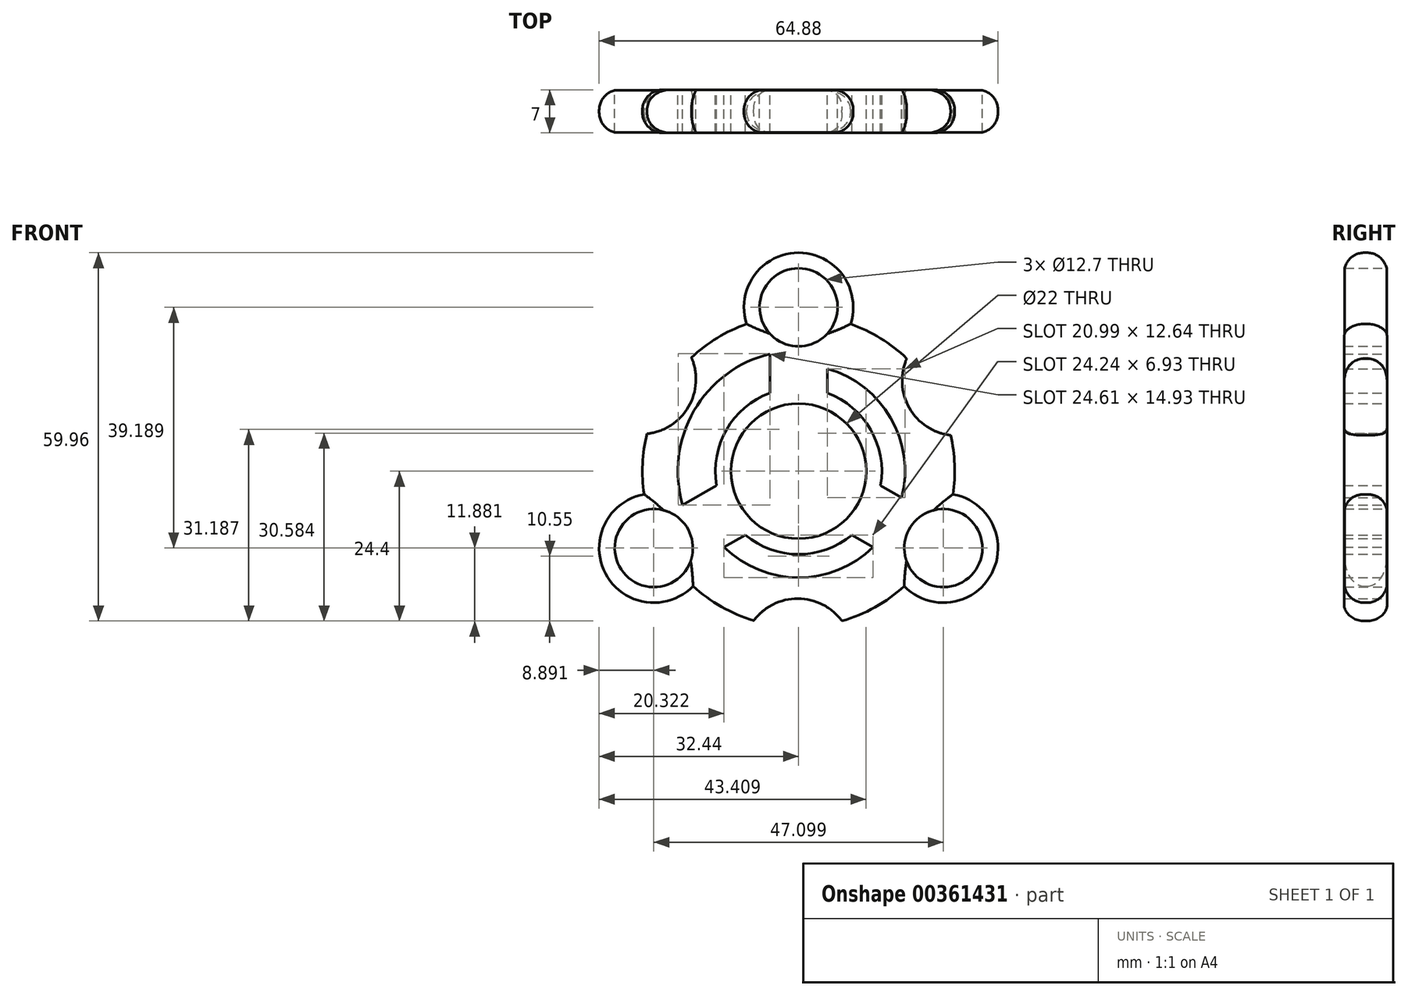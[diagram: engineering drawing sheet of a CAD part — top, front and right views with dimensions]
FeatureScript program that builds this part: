
annotation { "Feature Type Name" : "Feature", "Feature Type Description" : "" }
export const myFeature = defineFeature(function(context is Context, id is Id, definition is map)
    precondition{}
    {
        {
            var Q0;
            Q0=qCreatedBy(makeId("Front.planeOp"),FACE);
            var sketch = newSketch(context, id + "F0", { "sketchPlane" : qUnion([Q0])});
            skCircle(sketch, "E0", {"center": v(0, 0) * mm, "radius": 11 * mm});
            skCircle(sketch, "E1", {"center": v(0, 0) * mm, "radius": 25.4 * mm});
            skCircle(sketch, "E2", {"center": v(-23.55, -12.52) * mm, "radius": 6.35 * mm});
            skCircle(sketch, "E3", {"center": v(-23.55, -12.52) * mm, "radius": 8.9 * mm});
            skCircle(sketch, "E4", {"center": v(23.55, -12.52) * mm, "radius": 6.35 * mm});
            skCircle(sketch, "E5", {"center": v(23.55, -12.52) * mm, "radius": 8.9 * mm});
            skCircle(sketch, "E6", {"center": v(0, 26.67) * mm, "radius": 6.35 * mm});
            skCircle(sketch, "E7", {"center": v(0, 26.67) * mm, "radius": 8.9 * mm});
            skCircle(sketch, "E8", {"center": v(0, 0) * mm, "radius": 52.92 * mm});
            skCircle(sketch, "E9", {"center": v(0, 0) * mm, "radius": 35.56 * mm});
            skCircle(sketch, "E10", {"center": v(0, 0) * mm, "radius": 19.65 * mm});
            skCircle(sketch, "E11", {"center": v(0, 0) * mm, "radius": 17.32 * mm});
            skLineSegment(sketch, "E12", {"start": v(-4.65, 19.1) * mm, "end": v(-4.65, 9.97) * mm});
            skLineSegment(sketch, "E13", {"start": v(0, 0) * mm, "end": v(0, 14.53) * mm});
            skLineSegment(sketch, "E14.MirrorCS", {"start": v(4.65, 19.1) * mm, "end": v(4.65, 9.97) * mm});
            skLineSegment(sketch, "E15.1.0", {"start": v(-14.21, -13.57) * mm, "end": v(-6.3, -9.01) * mm});
            skLineSegment(sketch, "E15.1.1", {"start": v(-18.86, -5.52) * mm, "end": v(-10.96, -0.96) * mm});
            skLineSegment(sketch, "E15.2.0", {"start": v(18.86, -5.52) * mm, "end": v(10.96, -0.96) * mm});
            skLineSegment(sketch, "E15.2.1", {"start": v(14.21, -13.57) * mm, "end": v(6.3, -9.01) * mm});
            skCircle(sketch, "E16.0", {"center": v(0, 0) * mm, "radius": 13.54 * mm});
            skCircle(sketch, "E17", {"center": v(25.75, 14.7) * mm, "radius": 8.92 * mm});
            skCircle(sketch, "E18.1.0", {"center": v(-25.61, 14.95) * mm, "radius": 8.92 * mm});
            skCircle(sketch, "E18.2.0", {"center": v(-0.14, -29.66) * mm, "radius": 8.92 * mm});
            skSolve(sketch);
        }
        {
            var Q0;
            Q0=makeQuery(id+"F0.imprint","IMPRINT",FACE,{"disambiguationData":[TD([[makeQuery(id+"F0.imprint","IMPRINT",EDGE,{"derivedFrom":sQuery(id+"F0.wireOp",EDGE,"mSKZXrSF-bokL-tN16-Lumc-55fyRWtqHddJ")}),-1.0]])]});
            var Q1;
            {var subQ8=sQuery(id+"F0.wireOp",EDGE,"fPu7WKpn-9iuT-SH4j-aVLn-gu6anXdCReWU");Q1=makeQuery(id+"F0.imprint","IMPRINT",FACE,{"disambiguationData":[TD([[makeQuery(id+"F0.imprint","IMPRINT",EDGE,{"derivedFrom":subQ8}),1.0]])]});}
            var Q2;
            {var subQ3=sQuery(id+"F0.wireOp",EDGE,"4ilAvNyg-G02q-2Sgi-f1XK-hpsLkyDSZg0P");Q2=makeQuery(id+"F0.imprint","IMPRINT",FACE,{"disambiguationData":[TD([[makeQuery(id+"F0.imprint","IMPRINT",EDGE,{"derivedFrom":subQ3}),-1.0]])]});}
            var Q3;
            {var subQ0=sQuery(id+"F0.wireOp",EDGE,"f3iT29FV-d3kl-SGgA-KpPZ-BqzFadvLnQMr");var subQ1=sQuery(id+"F0.wireOp",EDGE,"k1AMuMOI-9OIa-mogb-beaB-4OQdduFXYsJP");var subQ2=makeQuery(id+"F0.imprint","INTERSECT",VERTEX,{"derivedFrom":[subQ1,subQ0]});Q3=makeQuery(id+"F0.imprint","IMPRINT",FACE,{"disambiguationData":[TD([[makeQuery(id+"F0.imprint","IMPRINT",EDGE,{"disambiguationData":[TD([[subQ2,-1.0]])],"derivedFrom":subQ1}),1.0]])]});}
            var Q4;
            {var subQ0=sQuery(id+"F0.wireOp",EDGE,"k1AMuMOI-9OIa-mogb-beaB-4OQdduFXYsJP");var subQ1=sQuery(id+"F0.wireOp",EDGE,"iGLwzaDJ-7IT3-vr1I-QoHF-4tAO6eRJBZaL");var subQ2=makeQuery(id+"F0.imprint","INTERSECT",VERTEX,{"disambiguationData":[OD(0.0)],"derivedFrom":[subQ1,subQ0]});Q4=makeQuery(id+"F0.imprint","IMPRINT",FACE,{"disambiguationData":[TD([[makeQuery(id+"F0.imprint","IMPRINT",EDGE,{"disambiguationData":[TD([[subQ2,-1.0]])],"derivedFrom":subQ1}),1.0]])]});}
            var Q5;
            {var subQ0=sQuery(id+"F0.wireOp",EDGE,"F0ToaT1C-rCX3-ocJg-bCzJ-bWa1iAX8OkwY");var subQ1=sQuery(id+"F0.wireOp",EDGE,"iGLwzaDJ-7IT3-vr1I-QoHF-4tAO6eRJBZaL");var subQ2=makeQuery(id+"F0.imprint","INTERSECT",VERTEX,{"disambiguationData":[OD(1.0)],"derivedFrom":[subQ1,subQ0]});Q5=makeQuery(id+"F0.imprint","IMPRINT",FACE,{"disambiguationData":[TD([[makeQuery(id+"F0.imprint","IMPRINT",EDGE,{"disambiguationData":[TD([[subQ2,-1.0]])],"derivedFrom":subQ1}),1.0]])]});}
            var Q6;
            {var subQ0=sQuery(id+"F0.wireOp",EDGE,"k1AMuMOI-9OIa-mogb-beaB-4OQdduFXYsJP");var subQ2=sQuery(id+"F0.wireOp",EDGE,"iGLwzaDJ-7IT3-vr1I-QoHF-4tAO6eRJBZaL");var subQ3=makeQuery(id+"F0.imprint","INTERSECT",VERTEX,{"disambiguationData":[OD(0.0)],"derivedFrom":[subQ2,subQ0]});Q6=makeQuery(id+"F0.imprint","IMPRINT",FACE,{"disambiguationData":[TD([[makeQuery(id+"F0.imprint","IMPRINT",EDGE,{"disambiguationData":[TD([[subQ3,-1.0]])],"derivedFrom":subQ2}),-1.0]])]});}
            var Q7;
            {var subQ0=sQuery(id+"F0.wireOp",EDGE,"Pe8qA6hG-RcvW-RrlY-0SVl-eZSLoO9VlF4p");Q7=makeQuery(id+"F0.imprint","IMPRINT",FACE,{"disambiguationData":[TD([[makeQuery(id+"F0.imprint","IMPRINT",EDGE,{"derivedFrom":subQ0}),1.0]])]});}
            var Q8;
            {var subQ3=sQuery(id+"F0.wireOp",EDGE,"SQ3UOjtt-CO0L-W6pf-Tdd5-0RniTD11PeOA");Q8=makeQuery(id+"F0.imprint","IMPRINT",FACE,{"disambiguationData":[TD([[makeQuery(id+"F0.imprint","IMPRINT",EDGE,{"derivedFrom":subQ3}),-1.0]])]});}
            var Q9;
            {var subQ0=sQuery(id+"F0.wireOp",EDGE,"4dQ9Bq4I-DzAn-Wkjs-vgun-b56G0d8Tkzou");Q9=makeQuery(id+"F0.imprint","IMPRINT",FACE,{"disambiguationData":[TD([[makeQuery(id+"F0.imprint","IMPRINT",EDGE,{"derivedFrom":subQ0}),1.0]])]});}
            var Q10;
            {var subQ3=sQuery(id+"F0.wireOp",EDGE,"QSqqfJXS-DOuh-B992-D5fL-yo85PLpnEcZw");Q10=makeQuery(id+"F0.imprint","IMPRINT",FACE,{"disambiguationData":[TD([[makeQuery(id+"F0.imprint","IMPRINT",EDGE,{"derivedFrom":subQ3}),-1.0]])]});}
            var Q11;
            {var subQ0=sQuery(id+"F0.wireOp",EDGE,"SBCOgly3-Q38N-qhpe-h8m8-IKpbl3d7nyb5");var subQ1=sQuery(id+"F0.wireOp",EDGE,"XELYKncj-OPtR-12Rn-Jsxf-ExqIg9yh0c7n");var subQ2=makeQuery(id+"F0.imprint","INTERSECT",VERTEX,{"derivedFrom":[subQ1,subQ0]});Q11=makeQuery(id+"F0.imprint","IMPRINT",FACE,{"disambiguationData":[TD([[makeQuery(id+"F0.imprint","IMPRINT",EDGE,{"disambiguationData":[TD([[subQ2,-1.0]])],"derivedFrom":subQ1}),1.0]])]});}
            var Q12;
            {var subQ0=sQuery(id+"F0.wireOp",EDGE,"f3iT29FV-d3kl-SGgA-KpPZ-BqzFadvLnQMr");var subQ1=sQuery(id+"F0.wireOp",EDGE,"8PpJuGD2-E3kl-GQEw-ypm4-Vkr7KxbCOpBG");var subQ2=makeQuery(id+"F0.imprint","INTERSECT",VERTEX,{"derivedFrom":[subQ1,subQ0]});Q12=makeQuery(id+"F0.imprint","IMPRINT",FACE,{"disambiguationData":[TD([[makeQuery(id+"F0.imprint","IMPRINT",EDGE,{"disambiguationData":[TD([[subQ2,1.0]])],"derivedFrom":subQ1}),1.0]])]});}
            var Q13;
            {var subQ0=sQuery(id+"F0.wireOp",EDGE,"FViSIV4C-5KW0-IByP-Mo0J-ua9ajbXaziPq");var subQ1=sQuery(id+"F0.wireOp",EDGE,"iGLwzaDJ-7IT3-vr1I-QoHF-4tAO6eRJBZaL");var subQ2=makeQuery(id+"F0.imprint","INTERSECT",VERTEX,{"disambiguationData":[OD(1.0)],"derivedFrom":[subQ1,subQ0]});Q13=makeQuery(id+"F0.imprint","IMPRINT",FACE,{"disambiguationData":[TD([[makeQuery(id+"F0.imprint","IMPRINT",EDGE,{"disambiguationData":[TD([[subQ2,-1.0]])],"derivedFrom":subQ1}),1.0]])]});}
            var Q14;
            {var subQ0=sQuery(id+"F0.wireOp",EDGE,"XELYKncj-OPtR-12Rn-Jsxf-ExqIg9yh0c7n");var subQ1=sQuery(id+"F0.wireOp",EDGE,"iGLwzaDJ-7IT3-vr1I-QoHF-4tAO6eRJBZaL");var subQ2=makeQuery(id+"F0.imprint","INTERSECT",VERTEX,{"disambiguationData":[OD(0.0)],"derivedFrom":[subQ1,subQ0]});Q14=makeQuery(id+"F0.imprint","IMPRINT",FACE,{"disambiguationData":[TD([[makeQuery(id+"F0.imprint","IMPRINT",EDGE,{"disambiguationData":[TD([[subQ2,-1.0]])],"derivedFrom":subQ1}),1.0]])]});}
            var Q15;
            Q15=makeQuery(id+"F0.imprint","IMPRINT",FACE,{"disambiguationData":[TD([[makeQuery(id+"F0.imprint","IMPRINT",EDGE,{"derivedFrom":sQuery(id+"F0.wireOp",EDGE,"1c7fcd95-4264-435f-8558-640e4e192e05.1.0")}),-1.0]])]});
            var Q16;
            Q16=makeQuery(id+"F0.imprint","IMPRINT",FACE,{"disambiguationData":[TD([[makeQuery(id+"F0.imprint","IMPRINT",EDGE,{"derivedFrom":sQuery(id+"F0.wireOp",EDGE,"30GUSKW5-8Tkx-gIO0-MBQh-iSdmt1q3Aj4F")}),-1.0]])]});
            var Q17;
            {var subQ0=sQuery(id+"F0.wireOp",EDGE,"8PpJuGD2-E3kl-GQEw-ypm4-Vkr7KxbCOpBG");var subQ1=sQuery(id+"F0.wireOp",EDGE,"iGLwzaDJ-7IT3-vr1I-QoHF-4tAO6eRJBZaL");var subQ2=makeQuery(id+"F0.imprint","INTERSECT",VERTEX,{"disambiguationData":[OD(0.0)],"derivedFrom":[subQ1,subQ0]});Q17=makeQuery(id+"F0.imprint","IMPRINT",FACE,{"disambiguationData":[TD([[makeQuery(id+"F0.imprint","IMPRINT",EDGE,{"disambiguationData":[TD([[subQ2,-1.0]])],"derivedFrom":subQ1}),1.0]])]});}
            var Q18;
            {var subQ0=sQuery(id+"F0.wireOp",EDGE,"8PpJuGD2-E3kl-GQEw-ypm4-Vkr7KxbCOpBG");var subQ2=sQuery(id+"F0.wireOp",EDGE,"iGLwzaDJ-7IT3-vr1I-QoHF-4tAO6eRJBZaL");var subQ4=makeQuery(id+"F0.imprint","INTERSECT",VERTEX,{"disambiguationData":[OD(0.0)],"derivedFrom":[subQ2,subQ0]});Q18=makeQuery(id+"F0.imprint","IMPRINT",FACE,{"disambiguationData":[TD([[makeQuery(id+"F0.imprint","IMPRINT",EDGE,{"disambiguationData":[TD([[subQ4,-1.0]])],"derivedFrom":subQ2}),-1.0]])]});}
            var Q19;
            {var subQ0=sQuery(id+"F0.wireOp",EDGE,"XELYKncj-OPtR-12Rn-Jsxf-ExqIg9yh0c7n");var subQ2=sQuery(id+"F0.wireOp",EDGE,"iGLwzaDJ-7IT3-vr1I-QoHF-4tAO6eRJBZaL");var subQ6=makeQuery(id+"F0.imprint","INTERSECT",VERTEX,{"disambiguationData":[OD(0.0)],"derivedFrom":[subQ2,subQ0]});Q19=makeQuery(id+"F0.imprint","IMPRINT",FACE,{"disambiguationData":[TD([[makeQuery(id+"F0.imprint","IMPRINT",EDGE,{"disambiguationData":[TD([[subQ6,-1.0]])],"derivedFrom":subQ2}),-1.0]])]});}
            var Q20;
            {var subQ0=sQuery(id+"F0.wireOp",EDGE,"aqUmptsU-d8FQ-e8lO-tFD0-okvlk6A5uSeS");var subQ1=sQuery(id+"F0.wireOp",EDGE,"iGLwzaDJ-7IT3-vr1I-QoHF-4tAO6eRJBZaL");var subQ2=makeQuery(id+"F0.imprint","INTERSECT",VERTEX,{"disambiguationData":[OD(1.0)],"derivedFrom":[subQ1,subQ0]});Q20=makeQuery(id+"F0.imprint","IMPRINT",FACE,{"disambiguationData":[TD([[makeQuery(id+"F0.imprint","IMPRINT",EDGE,{"disambiguationData":[TD([[subQ2,-1.0]])],"derivedFrom":subQ1}),1.0]])]});}
            var Q21;
            {var subQ1=sQuery(id+"F0.wireOp",EDGE,"iGLwzaDJ-7IT3-vr1I-QoHF-4tAO6eRJBZaL");var subQ8=makeQuery(id+"F0.imprint","INTERSECT",VERTEX,{"derivedFrom":[subQ1,sQuery(id+"F0.wireOp",EDGE,"1c7fcd95-4264-435f-8558-640e4e192e05.2.3")]});Q21=makeQuery(id+"F0.imprint","IMPRINT",FACE,{"disambiguationData":[TD([[makeQuery(id+"F0.imprint","IMPRINT",EDGE,{"disambiguationData":[TD([[subQ8,1.0]])],"derivedFrom":subQ1}),1.0]])]});}
            var Q22;
            {var subQ1=sQuery(id+"F0.wireOp",EDGE,"iGLwzaDJ-7IT3-vr1I-QoHF-4tAO6eRJBZaL");var subQ7=makeQuery(id+"F0.imprint","INTERSECT",VERTEX,{"derivedFrom":[subQ1,sQuery(id+"F0.wireOp",EDGE,"1c7fcd95-4264-435f-8558-640e4e192e05.1.3")]});Q22=makeQuery(id+"F0.imprint","IMPRINT",FACE,{"disambiguationData":[TD([[makeQuery(id+"F0.imprint","IMPRINT",EDGE,{"disambiguationData":[TD([[subQ7,1.0]])],"derivedFrom":subQ1}),1.0]])]});}
            var Q23;
            {var subQ1=sQuery(id+"F0.wireOp",EDGE,"iGLwzaDJ-7IT3-vr1I-QoHF-4tAO6eRJBZaL");var subQ5=makeQuery(id+"F0.imprint","INTERSECT",VERTEX,{"derivedFrom":[subQ1,sQuery(id+"F0.wireOp",EDGE,"MQ4H1yJi-5HLn-YdNj-5kv0-3AdfZDWRfWeK")]});Q23=makeQuery(id+"F0.imprint","IMPRINT",FACE,{"disambiguationData":[TD([[makeQuery(id+"F0.imprint","IMPRINT",EDGE,{"disambiguationData":[TD([[subQ5,1.0]])],"derivedFrom":subQ1}),1.0]])]});}
            var Q24;
            Q24=makeQuery(id+"F0.imprint","IMPRINT",FACE,{"disambiguationData":[TD([[makeQuery(id+"F0.imprint","IMPRINT",EDGE,{"derivedFrom":sQuery(id+"F0.wireOp",EDGE,"1c7fcd95-4264-435f-8558-640e4e192e05.2.0")}),-1.0]])]});
            var Q25;
            {var subQ0=sQuery(id+"F0.wireOp",EDGE,"k1AMuMOI-9OIa-mogb-beaB-4OQdduFXYsJP");var subQ1=sQuery(id+"F0.wireOp",EDGE,"iGLwzaDJ-7IT3-vr1I-QoHF-4tAO6eRJBZaL");var subQ2=makeQuery(id+"F0.imprint","INTERSECT",VERTEX,{"disambiguationData":[OD(1.0)],"derivedFrom":[subQ1,subQ0]});Q25=makeQuery(id+"F0.imprint","IMPRINT",FACE,{"disambiguationData":[TD([[makeQuery(id+"F0.imprint","IMPRINT",EDGE,{"disambiguationData":[TD([[subQ2,-1.0]])],"derivedFrom":subQ1}),1.0]])]});}
            var Q26;
            {var subQ0=sQuery(id+"F0.wireOp",EDGE,"k1AMuMOI-9OIa-mogb-beaB-4OQdduFXYsJP");var subQ1=sQuery(id+"F0.wireOp",EDGE,"iGLwzaDJ-7IT3-vr1I-QoHF-4tAO6eRJBZaL");var subQ2=makeQuery(id+"F0.imprint","INTERSECT",VERTEX,{"disambiguationData":[OD(0.0)],"derivedFrom":[subQ1,subQ0]});Q26=makeQuery(id+"F0.imprint","IMPRINT",FACE,{"disambiguationData":[TD([[makeQuery(id+"F0.imprint","IMPRINT",EDGE,{"disambiguationData":[TD([[subQ2,1.0]])],"derivedFrom":subQ1}),1.0]])]});}
            var Q27;
            Q27=makeQuery(id+"F0.imprint","IMPRINT",FACE,{"disambiguationData":[TD([[makeQuery(id+"F0.imprint","IMPRINT",EDGE,{"derivedFrom":sQuery(id+"F0.wireOp",EDGE,"E0")}),-1.0]])]});
            var Q28;
            {var subQ0=sQuery(id+"F0.wireOp",EDGE,"E7");var subQ1=sQuery(id+"F0.wireOp",EDGE,"E1");var subQ2=makeQuery(id+"F0.imprint","INTERSECT",VERTEX,{"disambiguationData":[OD(0.0)],"derivedFrom":[subQ1,subQ0]});Q28=makeQuery(id+"F0.imprint","IMPRINT",FACE,{"disambiguationData":[TD([[makeQuery(id+"F0.imprint","IMPRINT",EDGE,{"disambiguationData":[TD([[subQ2,-1.0]])],"derivedFrom":subQ1}),1.0]])]});}
            var Q29;
            {var subQ1=sQuery(id+"F0.wireOp",EDGE,"E1");var subQ4=sQuery(id+"F0.wireOp",EDGE,"E7");var subQ7=makeQuery(id+"F0.imprint","INTERSECT",VERTEX,{"disambiguationData":[OD(0.0)],"derivedFrom":[subQ1,subQ4]});Q29=makeQuery(id+"F0.imprint","IMPRINT",FACE,{"disambiguationData":[TD([[makeQuery(id+"F0.imprint","IMPRINT",EDGE,{"disambiguationData":[TD([[subQ7,-1.0]])],"derivedFrom":subQ1}),-1.0]])]});}
            var Q30;
            {var subQ0=sQuery(id+"F0.wireOp",EDGE,"786362c8-0dc7-4598-8f56-9a46119cb451");Q30=makeQuery(id+"F0.imprint","IMPRINT",FACE,{"disambiguationData":[TD([[makeQuery(id+"F0.imprint","IMPRINT",EDGE,{"derivedFrom":subQ0}),-1.0]])]});}
            var Q31;
            {var subQ0=sQuery(id+"F0.wireOp",EDGE,"E3");var subQ2=sQuery(id+"F0.wireOp",EDGE,"E1");var subQ3=makeQuery(id+"F0.imprint","INTERSECT",VERTEX,{"disambiguationData":[OD(0.0)],"derivedFrom":[subQ2,subQ0]});Q31=makeQuery(id+"F0.imprint","IMPRINT",FACE,{"disambiguationData":[TD([[makeQuery(id+"F0.imprint","IMPRINT",EDGE,{"disambiguationData":[TD([[subQ3,-1.0]])],"derivedFrom":subQ2}),-1.0]])]});}
            var Q32;
            {var subQ0=sQuery(id+"F0.wireOp",EDGE,"E3");var subQ1=sQuery(id+"F0.wireOp",EDGE,"E1");var subQ2=makeQuery(id+"F0.imprint","INTERSECT",VERTEX,{"disambiguationData":[OD(0.0)],"derivedFrom":[subQ1,subQ0]});Q32=makeQuery(id+"F0.imprint","IMPRINT",FACE,{"disambiguationData":[TD([[makeQuery(id+"F0.imprint","IMPRINT",EDGE,{"disambiguationData":[TD([[subQ2,-1.0]])],"derivedFrom":subQ1}),1.0]])]});}
            var Q33;
            {var subQ0=sQuery(id+"F0.wireOp",EDGE,"E5");var subQ2=sQuery(id+"F0.wireOp",EDGE,"E1");var subQ3=makeQuery(id+"F0.imprint","INTERSECT",VERTEX,{"disambiguationData":[OD(0.0)],"derivedFrom":[subQ2,subQ0]});Q33=makeQuery(id+"F0.imprint","IMPRINT",FACE,{"disambiguationData":[TD([[makeQuery(id+"F0.imprint","IMPRINT",EDGE,{"disambiguationData":[TD([[subQ3,-1.0]])],"derivedFrom":subQ2}),-1.0]])]});}
            var Q34;
            {var subQ0=sQuery(id+"F0.wireOp",EDGE,"E5");var subQ1=sQuery(id+"F0.wireOp",EDGE,"E1");var subQ2=makeQuery(id+"F0.imprint","INTERSECT",VERTEX,{"disambiguationData":[OD(0.0)],"derivedFrom":[subQ1,subQ0]});Q34=makeQuery(id+"F0.imprint","IMPRINT",FACE,{"disambiguationData":[TD([[makeQuery(id+"F0.imprint","IMPRINT",EDGE,{"disambiguationData":[TD([[subQ2,-1.0]])],"derivedFrom":subQ1}),1.0]])]});}
            var Q35;
            {var subQ0=sQuery(id+"F0.wireOp",EDGE,"234e8285-a1e6-4da0-a905-f59cf84429e6");Q35=makeQuery(id+"F0.imprint","IMPRINT",FACE,{"disambiguationData":[TD([[makeQuery(id+"F0.imprint","IMPRINT",EDGE,{"derivedFrom":subQ0}),-1.0]])]});}
            var Q36;
            {var subQ0=sQuery(id+"F0.wireOp",EDGE,"de03ec3f-5765-47dd-b776-27d281af80a7");Q36=makeQuery(id+"F0.imprint","IMPRINT",FACE,{"disambiguationData":[TD([[makeQuery(id+"F0.imprint","IMPRINT",EDGE,{"derivedFrom":subQ0}),-1.0]])]});}
            var Q37;
            {var subQ0=sQuery(id+"F0.wireOp",EDGE,"dw9GWBL9-mlah-X1e4-jjcR-aJVGEiCJIKLE");Q37=makeQuery(id+"F0.imprint","IMPRINT",FACE,{"disambiguationData":[TD([[makeQuery(id+"F0.imprint","IMPRINT",EDGE,{"derivedFrom":subQ0}),-1.0]])]});}
            var Q38;
            {var subQ0=sQuery(id+"F0.wireOp",EDGE,"f5477d1b-77a7-4964-8d89-f4b8eac2bd5f.1.0");Q38=makeQuery(id+"F0.imprint","IMPRINT",FACE,{"disambiguationData":[TD([[makeQuery(id+"F0.imprint","IMPRINT",EDGE,{"derivedFrom":subQ0}),-1.0]])]});}
            var Q39;
            {var subQ0=sQuery(id+"F0.wireOp",EDGE,"f5477d1b-77a7-4964-8d89-f4b8eac2bd5f.2.0");Q39=makeQuery(id+"F0.imprint","IMPRINT",FACE,{"disambiguationData":[TD([[makeQuery(id+"F0.imprint","IMPRINT",EDGE,{"derivedFrom":subQ0}),-1.0]])]});}
            var Q40;
            {var subQ0=sQuery(id+"F0.wireOp",EDGE,"9ed464e4-a16c-45d5-a885-2e48eb21a5a2.2.2");Q40=makeQuery(id+"F0.imprint","IMPRINT",FACE,{"disambiguationData":[TD([[makeQuery(id+"F0.imprint","IMPRINT",EDGE,{"derivedFrom":subQ0}),-1.0]])]});}
            var Q41;
            {var subQ0=sQuery(id+"F0.wireOp",EDGE,"4aeb8202-4e6b-4dbc-a32d-7e11a119f67a.2.1");Q41=makeQuery(id+"F0.imprint","IMPRINT",FACE,{"disambiguationData":[TD([[makeQuery(id+"F0.imprint","IMPRINT",EDGE,{"derivedFrom":subQ0}),-1.0]])]});}
            var Q42;
            {var subQ0=sQuery(id+"F0.wireOp",EDGE,"7f3ec712-6bbb-4074-be73-11f4e9898048.2.0");Q42=makeQuery(id+"F0.imprint","IMPRINT",FACE,{"disambiguationData":[TD([[makeQuery(id+"F0.imprint","IMPRINT",EDGE,{"derivedFrom":subQ0}),-1.0]])]});}
            var Q43;
            {var subQ0=sQuery(id+"F0.wireOp",EDGE,"c7a92ca6-c00c-4eda-bbf3-cb0ccd56349d.2.0");Q43=makeQuery(id+"F0.imprint","IMPRINT",FACE,{"disambiguationData":[TD([[makeQuery(id+"F0.imprint","IMPRINT",EDGE,{"derivedFrom":subQ0}),-1.0]])]});}
            var Q44;
            {var subQ0=sQuery(id+"F0.wireOp",EDGE,"E7");var subQ1=sQuery(id+"F0.wireOp",EDGE,"E1");var subQ2=makeQuery(id+"F0.imprint","INTERSECT",VERTEX,{"disambiguationData":[OD(1.0)],"derivedFrom":[subQ1,subQ0]});Q44=makeQuery(id+"F0.imprint","IMPRINT",FACE,{"disambiguationData":[TD([[makeQuery(id+"F0.imprint","IMPRINT",EDGE,{"disambiguationData":[TD([[subQ2,-1.0]])],"derivedFrom":subQ1}),1.0]])]});}
            var Q45;
            {var subQ0=sQuery(id+"F0.wireOp",EDGE,"E7");var subQ1=sQuery(id+"F0.wireOp",EDGE,"E1");var subQ2=makeQuery(id+"F0.imprint","INTERSECT",VERTEX,{"disambiguationData":[OD(0.0)],"derivedFrom":[subQ1,subQ0]});Q45=makeQuery(id+"F0.imprint","IMPRINT",FACE,{"disambiguationData":[TD([[makeQuery(id+"F0.imprint","IMPRINT",EDGE,{"disambiguationData":[TD([[subQ2,1.0]])],"derivedFrom":subQ1}),1.0]])]});}
            var Q46;
            {var subQ0=sQuery(id+"F0.wireOp",EDGE,"E3");var subQ1=sQuery(id+"F0.wireOp",EDGE,"E1");var subQ2=makeQuery(id+"F0.imprint","INTERSECT",VERTEX,{"disambiguationData":[OD(1.0)],"derivedFrom":[subQ1,subQ0]});Q46=makeQuery(id+"F0.imprint","IMPRINT",FACE,{"disambiguationData":[TD([[makeQuery(id+"F0.imprint","IMPRINT",EDGE,{"disambiguationData":[TD([[subQ2,-1.0]])],"derivedFrom":subQ1}),1.0]])]});}
            var Q47;
            {var subQ0=sQuery(id+"F0.wireOp",EDGE,"E15.2.0");var subQ1=sQuery(id+"F0.wireOp",EDGE,"E0");var subQ2=makeQuery(id+"F0.imprint","INTERSECT",VERTEX,{"derivedFrom":[subQ1,subQ0]});Q47=makeQuery(id+"F0.imprint","IMPRINT",FACE,{"disambiguationData":[TD([[makeQuery(id+"F0.imprint","IMPRINT",EDGE,{"disambiguationData":[TD([[subQ2,1.0]])],"derivedFrom":subQ1}),-1.0]])]});}
            var Q48;
            {var subQ0=sQuery(id+"F0.wireOp",EDGE,"E15.1.0");var subQ1=sQuery(id+"F0.wireOp",EDGE,"E0");var subQ2=makeQuery(id+"F0.imprint","INTERSECT",VERTEX,{"derivedFrom":[subQ1,subQ0]});Q48=makeQuery(id+"F0.imprint","IMPRINT",FACE,{"disambiguationData":[TD([[makeQuery(id+"F0.imprint","IMPRINT",EDGE,{"disambiguationData":[TD([[subQ2,1.0]])],"derivedFrom":subQ1}),-1.0]])]});}
            var Q49;
            {var subQ1=sQuery(id+"F0.wireOp",EDGE,"E10");var subQ7=sQuery(id+"F0.wireOp",EDGE,"E3");var subQ8=makeQuery(id+"F0.imprint","INTERSECT",VERTEX,{"disambiguationData":[OD(0.0)],"derivedFrom":[subQ7,subQ1]});Q49=makeQuery(id+"F0.imprint","IMPRINT",FACE,{"disambiguationData":[TD([[makeQuery(id+"F0.imprint","IMPRINT",EDGE,{"disambiguationData":[TD([[subQ8,1.0]])],"derivedFrom":subQ7}),-1.0]])]});}
            var Q50;
            {var subQ1=sQuery(id+"F0.wireOp",EDGE,"E10");var subQ7=sQuery(id+"F0.wireOp",EDGE,"E5");var subQ9=makeQuery(id+"F0.imprint","INTERSECT",VERTEX,{"disambiguationData":[OD(0.0)],"derivedFrom":[subQ7,subQ1]});Q50=makeQuery(id+"F0.imprint","IMPRINT",FACE,{"disambiguationData":[TD([[makeQuery(id+"F0.imprint","IMPRINT",EDGE,{"disambiguationData":[TD([[subQ9,-1.0]])],"derivedFrom":subQ7}),-1.0]])]});}
            var Q51;
            {var subQ0=sQuery(id+"F0.wireOp",EDGE,"E10");var subQ1=sQuery(id+"F0.wireOp",EDGE,"E7");var subQ2=makeQuery(id+"F0.imprint","INTERSECT",VERTEX,{"derivedFrom":[subQ1,subQ0,sQuery(id+"F0.wireOp",EDGE,"E12")]});Q51=makeQuery(id+"F0.imprint","IMPRINT",FACE,{"disambiguationData":[TD([[makeQuery(id+"F0.imprint","IMPRINT",EDGE,{"disambiguationData":[TD([[subQ2,-1.0]])],"derivedFrom":subQ1}),1.0]])]});}
            var Q52;
            {var subQ0=sQuery(id+"F0.wireOp",EDGE,"E12");var subQ6=sQuery(id+"F0.wireOp",EDGE,"E11");var subQ8=makeQuery(id+"F0.imprint","INTERSECT",VERTEX,{"derivedFrom":[subQ6,subQ0]});Q52=makeQuery(id+"F0.imprint","IMPRINT",FACE,{"disambiguationData":[TD([[makeQuery(id+"F0.imprint","IMPRINT",EDGE,{"disambiguationData":[TD([[subQ8,1.0]])],"derivedFrom":subQ6}),-1.0]])]});}
            var Q53;
            {var subQ0=sQuery(id+"F0.wireOp",EDGE,"E15.1.0");var subQ1=sQuery(id+"F0.wireOp",EDGE,"E10");var subQ2=makeQuery(id+"F0.imprint","INTERSECT",VERTEX,{"derivedFrom":[subQ1,subQ0]});Q53=makeQuery(id+"F0.imprint","IMPRINT",FACE,{"disambiguationData":[TD([[makeQuery(id+"F0.imprint","IMPRINT",EDGE,{"disambiguationData":[TD([[subQ2,-1.0]])],"derivedFrom":subQ1}),1.0]])]});}
            var Q54;
            {var subQ0=sQuery(id+"F0.wireOp",EDGE,"E15.2.0");var subQ1=sQuery(id+"F0.wireOp",EDGE,"E5");var subQ2=makeQuery(id+"F0.imprint","INTERSECT",VERTEX,{"derivedFrom":[subQ1,subQ0]});Q54=makeQuery(id+"F0.imprint","IMPRINT",FACE,{"disambiguationData":[TD([[makeQuery(id+"F0.imprint","IMPRINT",EDGE,{"disambiguationData":[TD([[subQ2,-1.0]])],"derivedFrom":subQ1}),1.0]])]});}
            var Q55;
            {var subQ3=sQuery(id+"F0.wireOp",EDGE,"E15.2.0");var subQ5=sQuery(id+"F0.wireOp",EDGE,"E5");var subQ6=makeQuery(id+"F0.imprint","INTERSECT",VERTEX,{"derivedFrom":[subQ5,subQ3]});Q55=makeQuery(id+"F0.imprint","IMPRINT",FACE,{"disambiguationData":[TD([[makeQuery(id+"F0.imprint","IMPRINT",EDGE,{"disambiguationData":[TD([[subQ6,-1.0]])],"derivedFrom":subQ5}),-1.0]])]});}
            var Q56;
            {var subQ0=sQuery(id+"F0.wireOp",EDGE,"E15.1.1");var subQ1=sQuery(id+"F0.wireOp",EDGE,"E3");var subQ2=makeQuery(id+"F0.imprint","INTERSECT",VERTEX,{"derivedFrom":[subQ1,subQ0]});Q56=makeQuery(id+"F0.imprint","IMPRINT",FACE,{"disambiguationData":[TD([[makeQuery(id+"F0.imprint","IMPRINT",EDGE,{"disambiguationData":[TD([[subQ2,1.0]])],"derivedFrom":subQ1}),1.0]])]});}
            var Q57;
            {var subQ0=sQuery(id+"F0.wireOp",EDGE,"E15.1.1");var subQ5=sQuery(id+"F0.wireOp",EDGE,"E3");var subQ6=makeQuery(id+"F0.imprint","INTERSECT",VERTEX,{"derivedFrom":[subQ5,subQ0]});Q57=makeQuery(id+"F0.imprint","IMPRINT",FACE,{"disambiguationData":[TD([[makeQuery(id+"F0.imprint","IMPRINT",EDGE,{"disambiguationData":[TD([[subQ6,1.0]])],"derivedFrom":subQ5}),-1.0]])]});}
            var Q58;
            {var subQ0=sQuery(id+"F0.wireOp",EDGE,"E10");var subQ1=sQuery(id+"F0.wireOp",EDGE,"E3");var subQ2=makeQuery(id+"F0.imprint","INTERSECT",VERTEX,{"disambiguationData":[OD(0.0)],"derivedFrom":[subQ1,subQ0]});Q58=makeQuery(id+"F0.imprint","IMPRINT",FACE,{"disambiguationData":[TD([[makeQuery(id+"F0.imprint","IMPRINT",EDGE,{"disambiguationData":[TD([[subQ2,1.0]])],"derivedFrom":subQ1}),1.0]])]});}
            var Q59;
            {var subQ0=sQuery(id+"F0.wireOp",EDGE,"E10");var subQ1=sQuery(id+"F0.wireOp",EDGE,"E5");var subQ2=makeQuery(id+"F0.imprint","INTERSECT",VERTEX,{"disambiguationData":[OD(0.0)],"derivedFrom":[subQ1,subQ0]});Q59=makeQuery(id+"F0.imprint","IMPRINT",FACE,{"disambiguationData":[TD([[makeQuery(id+"F0.imprint","IMPRINT",EDGE,{"disambiguationData":[TD([[subQ2,-1.0]])],"derivedFrom":subQ1}),1.0]])]});}
            var Q60;
            {var subQ1=sQuery(id+"F0.wireOp",EDGE,"E11");var subQ5=sQuery(id+"F0.wireOp",EDGE,"E12");var subQ6=makeQuery(id+"F0.imprint","INTERSECT",VERTEX,{"derivedFrom":[subQ1,subQ5]});Q60=makeQuery(id+"F0.imprint","IMPRINT",FACE,{"disambiguationData":[TD([[makeQuery(id+"F0.imprint","IMPRINT",EDGE,{"disambiguationData":[TD([[subQ6,1.0]])],"derivedFrom":subQ1}),1.0]])]});}
            var Q61;
            {var subQ0=sQuery(id+"F0.wireOp",EDGE,"E15.1.1");var subQ1=sQuery(id+"F0.wireOp",EDGE,"E11");var subQ2=makeQuery(id+"F0.imprint","INTERSECT",VERTEX,{"derivedFrom":[subQ1,subQ0]});Q61=makeQuery(id+"F0.imprint","IMPRINT",FACE,{"disambiguationData":[TD([[makeQuery(id+"F0.imprint","IMPRINT",EDGE,{"disambiguationData":[TD([[subQ2,-1.0]])],"derivedFrom":subQ1}),1.0]])]});}
            var Q62;
            {var subQ0=sQuery(id+"F0.wireOp",EDGE,"E15.2.1");var subQ1=sQuery(id+"F0.wireOp",EDGE,"E11");var subQ2=makeQuery(id+"F0.imprint","INTERSECT",VERTEX,{"derivedFrom":[subQ1,subQ0]});Q62=makeQuery(id+"F0.imprint","IMPRINT",FACE,{"disambiguationData":[TD([[makeQuery(id+"F0.imprint","IMPRINT",EDGE,{"disambiguationData":[TD([[subQ2,-1.0]])],"derivedFrom":subQ1}),1.0]])]});}
            extrude(context, id + "F1", {"entities" : qUnion([Q0, Q1, Q2, Q3, Q4, Q5, Q6, Q7, Q8, Q9, Q10, Q11, Q12, Q13, Q14, Q15, Q16, Q17, Q18, Q19, Q20, Q21, Q22, Q23, Q24, Q25, Q26, Q27, Q28, Q29, Q30, Q31, Q32, Q33, Q34, Q35, Q36, Q37, Q38, Q39, Q40, Q41, Q42, Q43, Q44, Q45, Q46, Q47, Q48, Q49, Q50, Q51, Q52, Q53, Q54, Q55, Q56, Q57, Q58, Q59, Q60, Q61, Q62]), "depth" : 7 * mm, "offsetDistance" : 25.4 * mm});
        }
        {
            var Q0;
            Q0=makeQuery(id+"F1.opExtrude","CAP_EDGE",EDGE,{"disambiguationData":[OSD([sQuery(id+"F0.wireOp",EDGE,"E3")])],"isStart":false});
            var Q1;
            Q1=makeQuery(id+"F1.opExtrude","CAP_EDGE",EDGE,{"disambiguationData":[OSD([sQuery(id+"F0.wireOp",EDGE,"E3")])],"isStart":true});
            var Q2;
            {var subQ0=sQuery(id+"F0.wireOp",EDGE,"E1");Q2=makeQuery(id+"F1.opExtrude","CAP_EDGE",EDGE,{"disambiguationData":[OSD([subQ0]),TDD([makeQuery(id+"F0.imprint","IMPRINT",EDGE,{"disambiguationData":[TD([[makeQuery(id+"F0.imprint","INTERSECT",VERTEX,{"derivedFrom":[subQ0,sQuery(id+"F0.wireOp",EDGE,"9ed464e4-a16c-45d5-a885-2e48eb21a5a2.2.3")]}),-1.0]])],"derivedFrom":subQ0})])],"isStart":false});}
            var Q3;
            Q3=makeQuery(id+"F1.opExtrude","CAP_EDGE",EDGE,{"disambiguationData":[OSD([sQuery(id+"F0.wireOp",EDGE,"E7")])],"isStart":false});
            var Q4;
            {var subQ0=sQuery(id+"F0.wireOp",EDGE,"E1");Q4=makeQuery(id+"F1.opExtrude","CAP_EDGE",EDGE,{"disambiguationData":[OSD([subQ0]),TDD([makeQuery(id+"F0.imprint","IMPRINT",EDGE,{"disambiguationData":[TD([[makeQuery(id+"F0.imprint","INTERSECT",VERTEX,{"derivedFrom":[subQ0,sQuery(id+"F0.wireOp",EDGE,"c7a92ca6-c00c-4eda-bbf3-cb0ccd56349d.2.3")]}),-1.0]])],"derivedFrom":subQ0})])],"isStart":false});}
            var Q5;
            {var subQ0=sQuery(id+"F0.wireOp",EDGE,"E1");Q5=makeQuery(id+"F1.opExtrude","CAP_EDGE",EDGE,{"disambiguationData":[OSD([subQ0]),TDD([makeQuery(id+"F0.imprint","IMPRINT",EDGE,{"disambiguationData":[TD([[makeQuery(id+"F0.imprint","INTERSECT",VERTEX,{"derivedFrom":[subQ0,sQuery(id+"F0.wireOp",EDGE,"c7a92ca6-c00c-4eda-bbf3-cb0ccd56349d.2.3")]}),-1.0]])],"derivedFrom":subQ0})])],"isStart":true});}
            var Q6;
            Q6=makeQuery(id+"F1.opExtrude","CAP_EDGE",EDGE,{"disambiguationData":[OSD([sQuery(id+"F0.wireOp",EDGE,"E7")])],"isStart":true});
            var Q7;
            Q7=makeQuery(id+"F1.opExtrude","CAP_EDGE",EDGE,{"disambiguationData":[OSD([sQuery(id+"F0.wireOp",EDGE,"c7a92ca6-c00c-4eda-bbf3-cb0ccd56349d.2.3")])],"isStart":false});
            var Q8;
            Q8=makeQuery(id+"F1.opExtrude","CAP_EDGE",EDGE,{"disambiguationData":[OSD([sQuery(id+"F0.wireOp",EDGE,"c7a92ca6-c00c-4eda-bbf3-cb0ccd56349d.2.3")])],"isStart":true});
            var Q9;
            Q9=makeQuery(id+"F1.opExtrude","CAP_EDGE",EDGE,{"disambiguationData":[OSD([sQuery(id+"F0.wireOp",EDGE,"c7a92ca6-c00c-4eda-bbf3-cb0ccd56349d.2.0")])],"isStart":false});
            var Q10;
            Q10=makeQuery(id+"F1.opExtrude","CAP_EDGE",EDGE,{"disambiguationData":[OSD([sQuery(id+"F0.wireOp",EDGE,"E5")])],"isStart":true});
            var Q11;
            {var subQ0=sQuery(id+"F0.wireOp",EDGE,"E1");Q11=makeQuery(id+"F1.opExtrude","CAP_EDGE",EDGE,{"disambiguationData":[OSD([subQ0]),TDD([makeQuery(id+"F0.imprint","IMPRINT",EDGE,{"disambiguationData":[TD([[makeQuery(id+"F0.imprint","INTERSECT",VERTEX,{"derivedFrom":[subQ0,sQuery(id+"F0.wireOp",EDGE,"4aeb8202-4e6b-4dbc-a32d-7e11a119f67a.2.3")]}),-1.0]])],"derivedFrom":subQ0})])],"isStart":true});}
            var Q12;
            {var subQ0=sQuery(id+"F0.wireOp",EDGE,"E1");Q12=makeQuery(id+"F1.opExtrude","CAP_EDGE",EDGE,{"disambiguationData":[OSD([subQ0]),TDD([makeQuery(id+"F0.imprint","IMPRINT",EDGE,{"disambiguationData":[TD([[makeQuery(id+"F0.imprint","INTERSECT",VERTEX,{"derivedFrom":[subQ0,sQuery(id+"F0.wireOp",EDGE,"4aeb8202-4e6b-4dbc-a32d-7e11a119f67a.2.3")]}),-1.0]])],"derivedFrom":subQ0})])],"isStart":false});}
            var Q13;
            {var subQ0=sQuery(id+"F0.wireOp",EDGE,"E1");Q13=makeQuery(id+"F1.opExtrude","CAP_EDGE",EDGE,{"disambiguationData":[OSD([subQ0]),TDD([makeQuery(id+"F0.imprint","IMPRINT",EDGE,{"disambiguationData":[TD([[makeQuery(id+"F0.imprint","INTERSECT",VERTEX,{"derivedFrom":[subQ0,sQuery(id+"F0.wireOp",EDGE,"9ed464e4-a16c-45d5-a885-2e48eb21a5a2.2.3")]}),-1.0]])],"derivedFrom":subQ0})])],"isStart":true});}
            var Q14;
            Q14=makeQuery(id+"F1.opExtrude","CAP_EDGE",EDGE,{"disambiguationData":[OSD([sQuery(id+"F0.wireOp",EDGE,"c7a92ca6-c00c-4eda-bbf3-cb0ccd56349d.2.0")])],"isStart":true});
            var Q15;
            Q15=makeQuery(id+"F1.opExtrude","CAP_EDGE",EDGE,{"disambiguationData":[OSD([sQuery(id+"F0.wireOp",EDGE,"E5")])],"isStart":false});
            fillet(context, id + "F2", {"entities" : qUnion([Q0, Q1, Q2, Q3, Q4, Q5, Q6, Q7, Q8, Q9, Q10, Q11, Q12, Q13, Q14, Q15]), "radius" : 3.3 * mm, "tangentPropagation" : true, "allowEdgeOverflow" : false});
        }
    });
